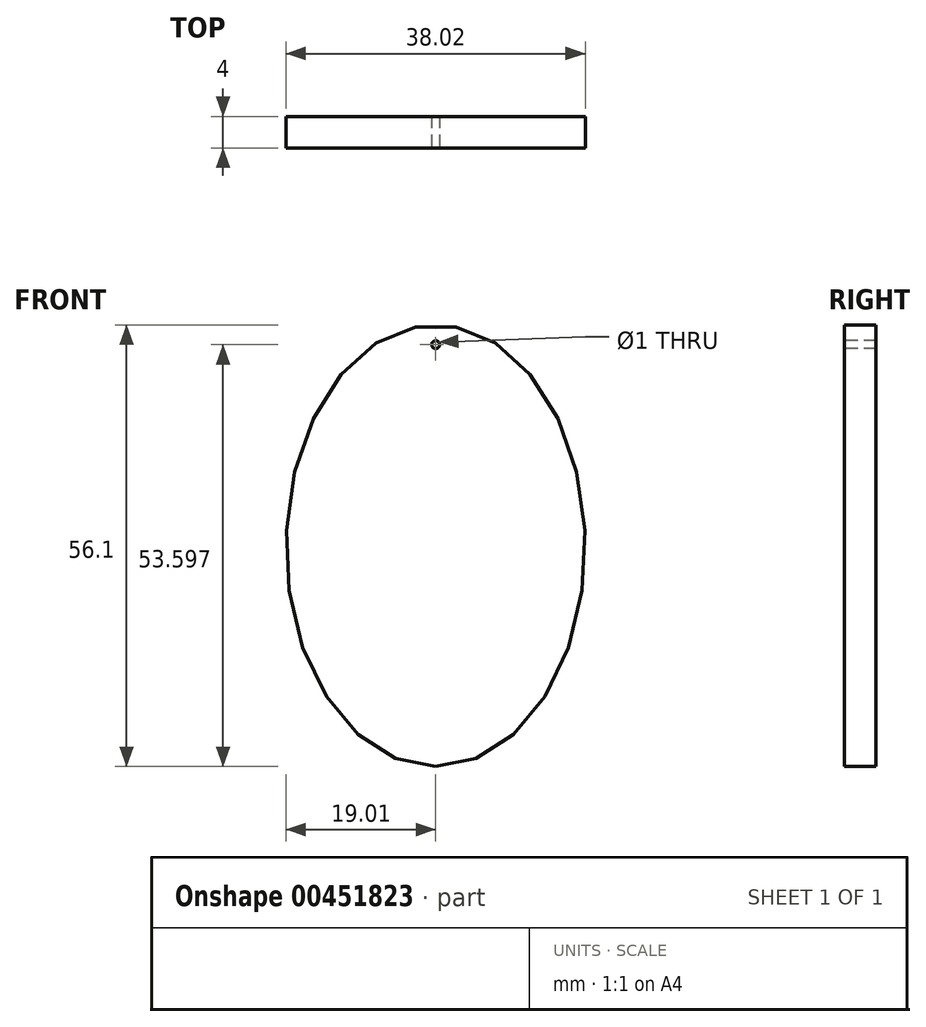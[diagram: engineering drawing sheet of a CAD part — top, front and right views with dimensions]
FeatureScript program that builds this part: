
annotation { "Feature Type Name" : "Feature", "Feature Type Description" : "" }
export const myFeature = defineFeature(function(context is Context, id is Id, definition is map)
    precondition{}
    {
        {
            var Q0;
            Q0=qCreatedBy(makeId("Front.planeOp"),FACE);
            var sketch = newSketch(context, id + "F0", { "sketchPlane" : qUnion([Q0])});
            skEllipse(sketch, "E0", {"center": v(0, 0) * mm, "majorRadius": 28.05 * mm, "minorRadius": 19 * mm, "majorAxis": v(0, -1)});
            skSolve(sketch);
        }
        {
            var Q0;
            Q0 = qSketchRegion(id + "F0", true);
            extrude(context, id + "F1", {"entities" : qUnion([Q0]), "endBound" : BoundingType.SYMMETRIC, "depth" : 4 * mm});
        }
        {
            var Q0;
            Q0=makeQuery(id+"F1.opExtrude","CAP_FACE",FACE,{"disambiguationData":[OSD([sQuery(id+"F0.wireOp",EDGE,"E0")])],"isStart":false});
            var sketch = newSketch(context, id + "F2", { "sketchPlane" : qUnion([Q0])});
            skLineSegment(sketch, "E1", {"start": v(0, 28.05) * mm, "end": v(0, 26.04) * mm});
            skLineSegment(sketch, "E2", {"start": v(0, 28.05) * mm, "end": v(0, 25.55) * mm});
            skSolve(sketch);
        }
        {
            var Q0;
            Q0=sQuery(id+"F2.wireOp",VERTEX,"E2.end");
            var Q1;
            Q1=makeQuery(id+"F1.opExtrude","SWEPT_BODY",BODY,{"disambiguationData":[OSD([sQuery(id+"F0.wireOp",EDGE,"E0")])]});
            hole(context, id + "F3", {"style" : HoleStyle.SIMPLE, "endStyle" : HoleEndStyle.THROUGH, "holeDiameter" : 1 * mm, "isTappedThrough" : true, "tappedDepth" : 12.7 * mm, "tapClearance" : 3, "locations" : qUnion([Q0]), "scope" : qUnion([Q1])});
        }
        {
            var Q0;
            Q0=makeQuery(id+"F1.opExtrude","SWEPT_BODY",BODY,{"disambiguationData":[OSD([sQuery(id+"F0.wireOp",EDGE,"E0")])]});
            transform(context, id + "F4", {"entities" : qUnion([Q0]), "transformType" : TransformType.TRANSLATION_3D, "dx" : 0 * mm, "dy" : 0 * mm, "dz" : 0 * mm, "makeCopy" : true});
        }
        {
            var Q0;
            Q0=makeQuery(id+"F4.opPattern","COPY",BODY,{"derivedFrom":makeQuery(id+"F1.opExtrude","SWEPT_BODY",BODY,{"disambiguationData":[OSD([sQuery(id+"F0.wireOp",EDGE,"E0")])]}),"instanceName":"1"});
            deleteBodies(context, id + "F5", {"entities" : qUnion([Q0])});
        }
    });
